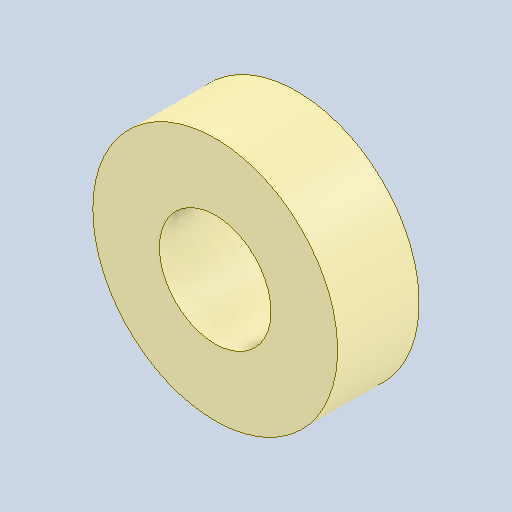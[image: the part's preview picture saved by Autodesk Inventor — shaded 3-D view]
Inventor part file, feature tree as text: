
AUTODESK INVENTOR PART (.ipt)
format: ipt  version: 2023 (Build 270158000, 158)  size: 103,424 bytes
history: native  units: in
note: dims shown in document units (in); Inventor stores cm internally (conversion verified against a paired STEP export)
features: extrude x1
ambient origin geometry x8: Origin, YZ Plane, XZ Plane, XY Plane, X Axis, Y Axis, Z Axis, Center Point
bodies: Solid1 (feature_tree)
feature tree (1):
  extrude  "Extrude1"  [1 undecoded]
note: 1 required parameter value undecoded (feature->parameter linkage not recoverable at this tier; creation-order binding heuristic only, values carry confidence <= 0.55)
